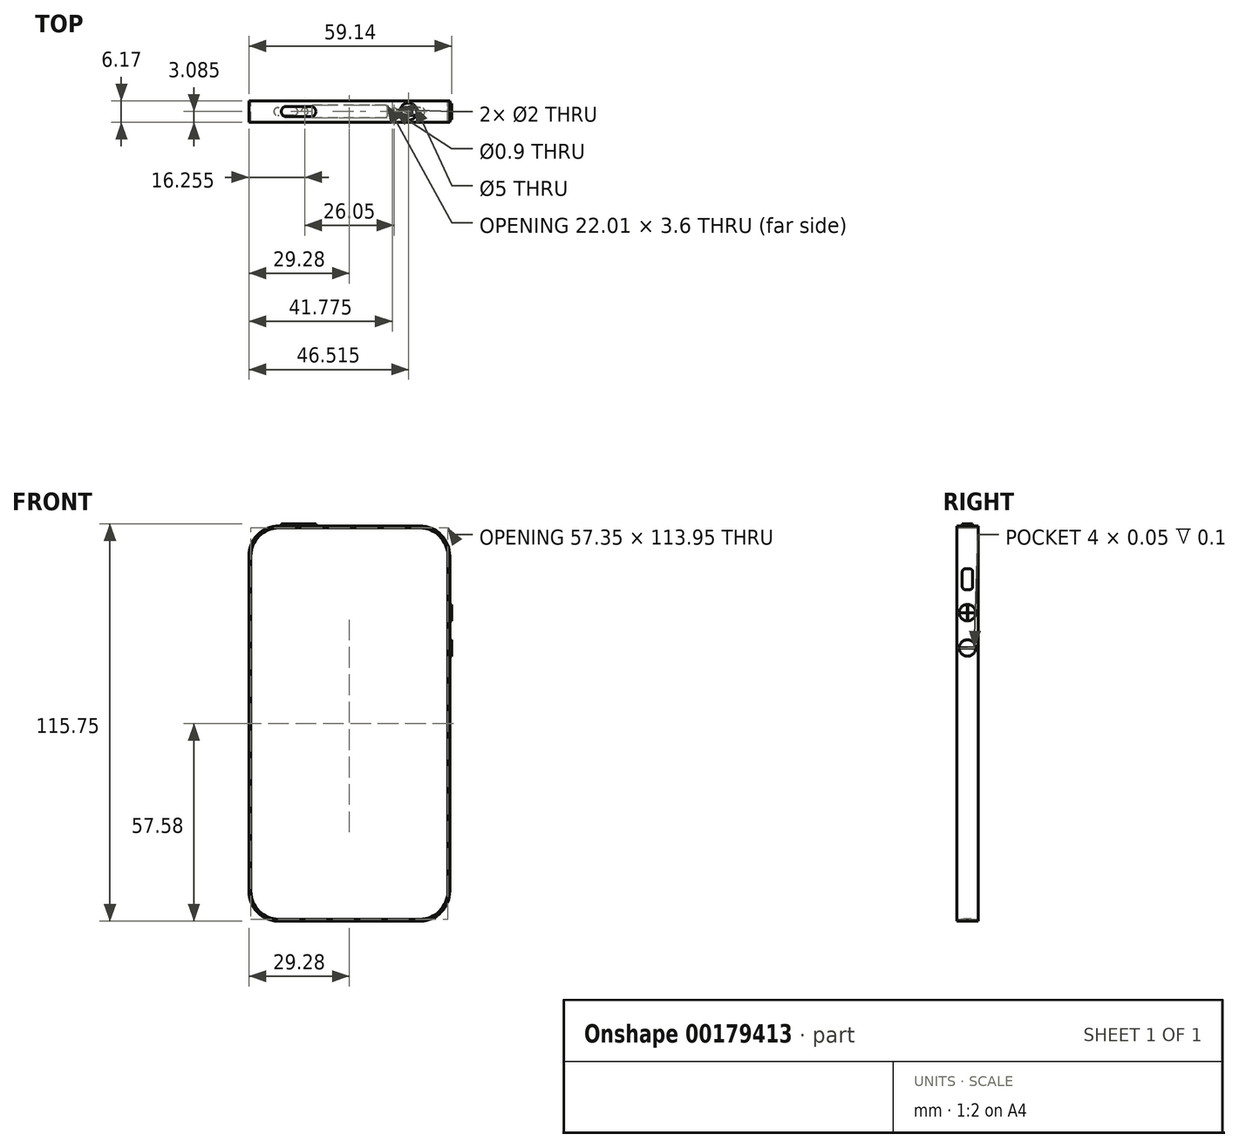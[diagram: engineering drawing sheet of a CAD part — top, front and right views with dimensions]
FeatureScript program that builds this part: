
annotation { "Feature Type Name" : "Feature", "Feature Type Description" : "" }
export const myFeature = defineFeature(function(context is Context, id is Id, definition is map)
    precondition{}
    {
        {
            var Q0;
            Q0=qCreatedBy(makeId("Front.planeOp"),FACE);
            var sketch = newSketch(context, id + "F0", { "sketchPlane" : qUnion([Q0])});
            skLineSegment(sketch, "E0.bottom", {"start": v(20.5, -57.58) * mm, "end": v(-20.5, -57.58) * mm});
            skLineSegment(sketch, "E0.top", {"start": v(20.5, 57.57) * mm, "end": v(-20.5, 57.57) * mm});
            skLineSegment(sketch, "E0.left", {"start": v(29.28, -48.8) * mm, "end": v(29.28, 48.8) * mm});
            skLineSegment(sketch, "E0.right", {"start": v(-29.28, -48.8) * mm, "end": v(-29.28, 48.8) * mm});
            skPoint(sketch, "E0.middle", {"position": v(0, 0) * mm});
            skLineSegment(sketch, "E1.bottom", {"start": v(20.5, -56.98) * mm, "end": v(-20.5, -56.97) * mm});
            skLineSegment(sketch, "E1.top", {"start": v(20.5, 56.98) * mm, "end": v(-20.5, 56.98) * mm});
            skLineSegment(sketch, "E1.left", {"start": v(28.67, -48.8) * mm, "end": v(28.68, 48.8) * mm});
            skLineSegment(sketch, "E1.right", {"start": v(-28.68, -48.8) * mm, "end": v(-28.68, 48.8) * mm});
            skPoint(sketch, "E2.visualSharp", {"position": v(-28.67, 56.97) * mm});
            skArc(sketch, "E2.filletArc", {"start": v(-20.5, 56.97) * mm, "mid": v(-26.28, 54.58) * mm, "end": v(-28.67, 48.8) * mm});
            skPoint(sketch, "E3.visualSharp", {"position": v(-29.28, 57.57) * mm});
            skArc(sketch, "E3.filletArc", {"start": v(-20.5, 57.57) * mm, "mid": v(-26.7, 55) * mm, "end": v(-29.27, 48.8) * mm});
            skPoint(sketch, "E4.visualSharp", {"position": v(28.68, 56.98) * mm});
            skArc(sketch, "E4.filletArc", {"start": v(28.68, 48.8) * mm, "mid": v(26.28, 54.58) * mm, "end": v(20.5, 56.97) * mm});
            skPoint(sketch, "E5.visualSharp", {"position": v(29.28, 57.57) * mm});
            skArc(sketch, "E5.filletArc", {"start": v(29.28, 48.8) * mm, "mid": v(26.7, 55) * mm, "end": v(20.5, 57.57) * mm});
            skPoint(sketch, "E6.visualSharp", {"position": v(-29.28, -57.58) * mm});
            skArc(sketch, "E6.filletArc", {"start": v(-29.28, -48.8) * mm, "mid": v(-26.7, -55) * mm, "end": v(-20.5, -57.57) * mm});
            skPoint(sketch, "E7.visualSharp", {"position": v(-28.68, -56.97) * mm});
            skArc(sketch, "E7.filletArc", {"start": v(-28.68, -48.8) * mm, "mid": v(-26.28, -54.58) * mm, "end": v(-20.5, -56.97) * mm});
            skPoint(sketch, "E8.visualSharp", {"position": v(29.28, -57.58) * mm});
            skArc(sketch, "E8.filletArc", {"start": v(20.5, -57.58) * mm, "mid": v(26.7, -55) * mm, "end": v(29.27, -48.8) * mm});
            skPoint(sketch, "E9.visualSharp", {"position": v(28.67, -56.98) * mm});
            skArc(sketch, "E9.filletArc", {"start": v(20.5, -56.98) * mm, "mid": v(26.28, -54.58) * mm, "end": v(28.67, -48.8) * mm});
            skSolve(sketch);
        }
        {
            var Q0;
            Q0=makeQuery(id+"F0.imprint","IMPRINT",FACE,{"disambiguationData":[TD([[makeQuery(id+"F0.imprint","IMPRINT",EDGE,{"derivedFrom":sQuery(id+"F0.wireOp",EDGE,"E0.bottom")}),-1.0]])]});
            extrude(context, id + "F1", {"entities" : qUnion([Q0]), "depth" : 6.17 * mm});
        }
        {
            var Q0;
            Q0=makeQuery(id+"F1.opExtrude","SWEPT_FACE",FACE,{"disambiguationData":[OSD([sQuery(id+"F0.wireOp",EDGE,"E0.left")])]});
            var sketch = newSketch(context, id + "F2", { "sketchPlane" : qUnion([Q0])});
            skLineSegment(sketch, "E10", {"start": v(-3.08, 48.8) * mm, "end": v(-3.08, -48.8) * mm, "construction": true});
            skCircle(sketch, "E11", {"center": v(-3.08, 32.3) * mm, "radius": 2.4 * mm});
            skCircle(sketch, "E12", {"center": v(-3.08, 22.01) * mm, "radius": 2.4 * mm});
            skLineSegment(sketch, "E13.bottom", {"start": v(-3.83, 45.04) * mm, "end": v(-2.33, 45.04) * mm});
            skLineSegment(sketch, "E13.top", {"start": v(-3.83, 39.04) * mm, "end": v(-2.33, 39.04) * mm});
            skLineSegment(sketch, "E13.left", {"start": v(-4.58, 44.3) * mm, "end": v(-4.58, 39.8) * mm});
            skLineSegment(sketch, "E13.right", {"start": v(-1.58, 44.3) * mm, "end": v(-1.58, 39.8) * mm});
            skPoint(sketch, "E14.visualSharp", {"position": v(-4.58, 45.04) * mm});
            skArc(sketch, "E14.filletArc", {"start": v(-3.83, 45.04) * mm, "mid": v(-4.37, 44.83) * mm, "end": v(-4.59, 44.3) * mm});
            skPoint(sketch, "E15.visualSharp", {"position": v(-1.58, 45.04) * mm});
            skArc(sketch, "E15.filletArc", {"start": v(-1.58, 44.3) * mm, "mid": v(-1.8, 44.83) * mm, "end": v(-2.33, 45.04) * mm});
            skPoint(sketch, "E16.visualSharp", {"position": v(-1.58, 39.04) * mm});
            skArc(sketch, "E16.filletArc", {"start": v(-2.33, 39.04) * mm, "mid": v(-1.8, 39.26) * mm, "end": v(-1.59, 39.8) * mm});
            skPoint(sketch, "E17.visualSharp", {"position": v(-4.58, 39.04) * mm});
            skArc(sketch, "E17.filletArc", {"start": v(-4.58, 39.8) * mm, "mid": v(-4.37, 39.26) * mm, "end": v(-3.83, 39.04) * mm});
            skSolve(sketch);
        }
        {
            var Q0;
            Q0=makeQuery(id+"F2.imprint","IMPRINT",FACE,{"disambiguationData":[TD([[makeQuery(id+"F2.imprint","IMPRINT",EDGE,{"derivedFrom":sQuery(id+"F2.wireOp",EDGE,"E13.bottom")}),-1.0]])]});
            extrude(context, id + "F3", {"entities" : qUnion([Q0]), "operationType" : NewBodyOperationType.REMOVE, "oppositeDirection" : true, "depth" : 0.55 * mm});
        }
        {
            var Q0;
            Q0=makeQuery(id+"F2.imprint","IMPRINT",FACE,{"disambiguationData":[TD([[makeQuery(id+"F2.imprint","IMPRINT",EDGE,{"derivedFrom":sQuery(id+"F2.wireOp",EDGE,"E11")}),1.0]])]});
            var Q1;
            Q1=makeQuery(id+"F2.imprint","IMPRINT",FACE,{"disambiguationData":[TD([[makeQuery(id+"F2.imprint","IMPRINT",EDGE,{"derivedFrom":sQuery(id+"F2.wireOp",EDGE,"E12")}),1.0]])]});
            extrude(context, id + "F4", {"entities" : qUnion([Q0, Q1]), "operationType" : NewBodyOperationType.ADD, "depth" : 0.58 * mm});
        }
        {
            var Q0;
            Q0=makeQuery(id+"F4.opExtrude","CAP_FACE",FACE,{"disambiguationData":[OSD([sQuery(id+"F2.wireOp",EDGE,"E11")])],"isStart":false});
            var sketch = newSketch(context, id + "F5", { "sketchPlane" : qUnion([Q0])});
            skLineSegment(sketch, "E18.bottom", {"start": v(-3.11, 30.3) * mm, "end": v(-3.06, 30.3) * mm});
            skLineSegment(sketch, "E18.top", {"start": v(-3.11, 34.3) * mm, "end": v(-3.06, 34.3) * mm});
            skLineSegment(sketch, "E18.left", {"start": v(-3.11, 30.3) * mm, "end": v(-3.11, 32.27) * mm});
            skLineSegment(sketch, "E18.right", {"start": v(-3.06, 30.3) * mm, "end": v(-3.06, 32.27) * mm});
            skPoint(sketch, "E18.middle", {"position": v(-3.08, 32.3) * mm});
            skLineSegment(sketch, "E19.bottom", {"start": v(-1.08, 32.27) * mm, "end": v(-3.06, 32.27) * mm});
            skLineSegment(sketch, "E19.top", {"start": v(-1.08, 32.32) * mm, "end": v(-3.06, 32.32) * mm});
            skLineSegment(sketch, "E19.left", {"start": v(-1.08, 32.27) * mm, "end": v(-1.08, 32.32) * mm});
            skLineSegment(sketch, "E19.right", {"start": v(-5.08, 32.27) * mm, "end": v(-5.08, 32.32) * mm});
            skLineSegment(sketch, "E20.trimOffspring", {"start": v(-3.11, 32.32) * mm, "end": v(-5.08, 32.32) * mm});
            skLineSegment(sketch, "E21.trimOffspring", {"start": v(-3.11, 32.32) * mm, "end": v(-3.11, 34.3) * mm});
            skLineSegment(sketch, "E22.trimOffspring", {"start": v(-3.06, 32.32) * mm, "end": v(-3.06, 34.3) * mm});
            skLineSegment(sketch, "E23.trimOffspring", {"start": v(-3.11, 32.27) * mm, "end": v(-5.08, 32.27) * mm});
            skSolve(sketch);
        }
        {
            var Q0;
            Q0=makeQuery(id+"F4.opExtrude","CAP_FACE",FACE,{"disambiguationData":[OSD([sQuery(id+"F2.wireOp",EDGE,"E12")])],"isStart":false});
            var sketch = newSketch(context, id + "F6", { "sketchPlane" : qUnion([Q0])});
            skLineSegment(sketch, "E24.bottom", {"start": v(-1.08, 21.99) * mm, "end": v(-5.08, 21.99) * mm});
            skLineSegment(sketch, "E24.top", {"start": v(-1.08, 22.04) * mm, "end": v(-5.08, 22.04) * mm});
            skLineSegment(sketch, "E24.left", {"start": v(-1.08, 21.99) * mm, "end": v(-1.08, 22.04) * mm});
            skLineSegment(sketch, "E24.right", {"start": v(-5.08, 21.99) * mm, "end": v(-5.08, 22.04) * mm});
            skPoint(sketch, "E24.middle", {"position": v(-3.08, 22.01) * mm});
            skSolve(sketch);
        }
        {
            var Q0;
            Q0=makeQuery(id+"F5.imprint","IMPRINT",FACE,{"disambiguationData":[TD([[makeQuery(id+"F5.imprint","IMPRINT",EDGE,{"derivedFrom":sQuery(id+"F5.wireOp",EDGE,"E18.bottom")}),1.0]])]});
            var Q1;
            Q1=makeQuery(id+"F6.imprint","IMPRINT",FACE,{"disambiguationData":[TD([[makeQuery(id+"F6.imprint","IMPRINT",EDGE,{"derivedFrom":sQuery(id+"F6.wireOp",EDGE,"E24.bottom")}),-1.0]])]});
            extrude(context, id + "F7", {"entities" : qUnion([Q0, Q1]), "operationType" : NewBodyOperationType.REMOVE, "oppositeDirection" : true, "depth" : 0.1 * mm});
        }
        {
            var Q0;
            Q0=makeQuery(id+"F1.opExtrude","SWEPT_FACE",FACE,{"disambiguationData":[OSD([sQuery(id+"F0.wireOp",EDGE,"E0.top")])]});
            var sketch = newSketch(context, id + "F8", { "sketchPlane" : qUnion([Q0])});
            skLineSegment(sketch, "E25", {"start": v(20.5, -3.08) * mm, "end": v(-20.5, -3.08) * mm, "construction": true});
            skCircle(sketch, "E26", {"center": v(17.24, -3.08) * mm, "radius": 2.5 * mm});
            skLineSegment(sketch, "E27.bottom", {"start": v(-18.33, -4.59) * mm, "end": v(-11.23, -4.59) * mm});
            skLineSegment(sketch, "E27.top", {"start": v(-18.33, -1.59) * mm, "end": v(-11.23, -1.59) * mm});
            skLineSegment(sketch, "E27.left", {"start": v(-19.83, -3.09) * mm, "end": v(-19.83, -3.09) * mm});
            skLineSegment(sketch, "E27.right", {"start": v(-9.73, -3.09) * mm, "end": v(-9.73, -3.09) * mm});
            skPoint(sketch, "E27.middle", {"position": v(-14.78, -3.09) * mm});
            skCircle(sketch, "E28", {"center": v(12.5, -3.09) * mm, "radius": 0.45 * mm});
            skPoint(sketch, "E29.visualSharp", {"position": v(-9.73, -4.59) * mm});
            skArc(sketch, "E29.filletArc", {"start": v(-11.23, -4.59) * mm, "mid": v(-10.17, -4.15) * mm, "end": v(-9.73, -3.09) * mm});
            skPoint(sketch, "E30.visualSharp", {"position": v(-9.73, -1.59) * mm});
            skArc(sketch, "E30.filletArc", {"start": v(-9.73, -3.09) * mm, "mid": v(-10.17, -2.02) * mm, "end": v(-11.23, -1.59) * mm});
            skPoint(sketch, "E31.visualSharp", {"position": v(-19.83, -4.59) * mm});
            skArc(sketch, "E31.filletArc", {"start": v(-19.83, -3.09) * mm, "mid": v(-19.4, -4.15) * mm, "end": v(-18.33, -4.59) * mm});
            skPoint(sketch, "E32.visualSharp", {"position": v(-19.83, -1.59) * mm});
            skArc(sketch, "E32.filletArc", {"start": v(-18.33, -1.59) * mm, "mid": v(-19.4, -2.02) * mm, "end": v(-19.83, -3.09) * mm});
            skSolve(sketch);
        }
        {
            var Q0;
            Q0=makeQuery(id+"F8.imprint","IMPRINT",FACE,{"disambiguationData":[TD([[makeQuery(id+"F8.imprint","IMPRINT",EDGE,{"derivedFrom":sQuery(id+"F8.wireOp",EDGE,"E26")}),1.0]])]});
            var Q1;
            Q1=makeQuery(id+"F8.imprint","IMPRINT",FACE,{"disambiguationData":[TD([[makeQuery(id+"F8.imprint","IMPRINT",EDGE,{"derivedFrom":sQuery(id+"F8.wireOp",EDGE,"E28")}),1.0]])]});
            var Q2;
            Q2=sQuery(id+"F8.wireOp",EDGE,"E26");
            var Q3;
            Q3=sQuery(id+"F8.wireOp",EDGE,"E28");
            extrude(context, id + "F9", {"entities" : qUnion([Q0, Q1]), "operationType" : NewBodyOperationType.REMOVE, "surfaceEntities" : qUnion([Q2, Q3]), "oppositeDirection" : true, "depth" : 0.6 * mm});
        }
        {
            var Q0;
            Q0=makeQuery(id+"F8.imprint","IMPRINT",FACE,{"disambiguationData":[TD([[makeQuery(id+"F8.imprint","IMPRINT",EDGE,{"derivedFrom":sQuery(id+"F8.wireOp",EDGE,"E27.bottom")}),1.0]])]});
            extrude(context, id + "F10", {"entities" : qUnion([Q0]), "operationType" : NewBodyOperationType.ADD, "depth" : 0.6 * mm});
        }
        {
            var Q0;
            Q0=makeQuery(id+"F1.opExtrude","SWEPT_FACE",FACE,{"disambiguationData":[OSD([sQuery(id+"F0.wireOp",EDGE,"E0.bottom")])]});
            var sketch = newSketch(context, id + "F11", { "sketchPlane" : qUnion([Q0])});
            skLineSegment(sketch, "E33", {"start": v(20.5, 3.08) * mm, "end": v(-20.5, 3.08) * mm, "construction": true});
            skLineSegment(sketch, "E34", {"start": v(0, 6.17) * mm, "end": v(0, 0) * mm, "construction": true});
            skLineSegment(sketch, "E35.bottom", {"start": v(10.5, 1.29) * mm, "end": v(-10.5, 1.28) * mm});
            skLineSegment(sketch, "E35.top", {"start": v(10.5, 4.89) * mm, "end": v(-10.5, 4.88) * mm});
            skLineSegment(sketch, "E35.left", {"start": v(11, 1.78) * mm, "end": v(11, 4.38) * mm});
            skLineSegment(sketch, "E35.right", {"start": v(-11, 1.78) * mm, "end": v(-11, 4.38) * mm});
            skPoint(sketch, "E35.middle", {"position": v(0, 3.08) * mm});
            skCircle(sketch, "E36", {"center": v(-13.03, 3.08) * mm, "radius": 1 * mm});
            skCircle(sketch, "E37", {"center": v(13.02, 3.08) * mm, "radius": 1 * mm});
            skLineSegment(sketch, "E38.bottom", {"start": v(-16.17, 1.94) * mm, "end": v(-20.84, 1.94) * mm});
            skLineSegment(sketch, "E38.top", {"start": v(-16.17, 4.24) * mm, "end": v(-20.84, 4.24) * mm});
            skLineSegment(sketch, "E38.left", {"start": v(-15.02, 3.09) * mm, "end": v(-15.02, 3.08) * mm});
            skLineSegment(sketch, "E38.right", {"start": v(-21.99, 3.09) * mm, "end": v(-21.99, 3.08) * mm});
            skPoint(sketch, "E38.middle", {"position": v(-18.5, 3.08) * mm});
            skLineSegment(sketch, "E39.bottom", {"start": v(20.83, 1.94) * mm, "end": v(16.16, 1.94) * mm});
            skLineSegment(sketch, "E39.top", {"start": v(20.83, 4.24) * mm, "end": v(16.16, 4.24) * mm});
            skLineSegment(sketch, "E39.left", {"start": v(21.98, 3.09) * mm, "end": v(21.98, 3.09) * mm});
            skLineSegment(sketch, "E39.right", {"start": v(15.01, 3.09) * mm, "end": v(15.01, 3.09) * mm});
            skPoint(sketch, "E39.middle", {"position": v(18.5, 3.08) * mm});
            skPoint(sketch, "E40.visualSharp", {"position": v(-15.02, 4.24) * mm});
            skArc(sketch, "E40.filletArc", {"start": v(-15.02, 3.08) * mm, "mid": v(-15.35, 3.9) * mm, "end": v(-16.17, 4.24) * mm});
            skPoint(sketch, "E41.visualSharp", {"position": v(-15.02, 1.94) * mm});
            skArc(sketch, "E41.filletArc", {"start": v(-16.17, 1.94) * mm, "mid": v(-15.35, 2.27) * mm, "end": v(-15.02, 3.09) * mm});
            skPoint(sketch, "E42.visualSharp", {"position": v(-21.99, 1.94) * mm});
            skArc(sketch, "E42.filletArc", {"start": v(-21.99, 3.09) * mm, "mid": v(-21.65, 2.27) * mm, "end": v(-20.84, 1.94) * mm});
            skPoint(sketch, "E43.visualSharp", {"position": v(-21.99, 4.24) * mm});
            skArc(sketch, "E43.filletArc", {"start": v(-20.84, 4.24) * mm, "mid": v(-21.65, 3.9) * mm, "end": v(-21.99, 3.08) * mm});
            skPoint(sketch, "E44.visualSharp", {"position": v(21.98, 4.24) * mm});
            skArc(sketch, "E44.filletArc", {"start": v(21.98, 3.09) * mm, "mid": v(21.65, 3.9) * mm, "end": v(20.83, 4.24) * mm});
            skPoint(sketch, "E45.visualSharp", {"position": v(21.98, 1.94) * mm});
            skArc(sketch, "E45.filletArc", {"start": v(20.83, 1.94) * mm, "mid": v(21.65, 2.27) * mm, "end": v(21.98, 3.09) * mm});
            skPoint(sketch, "E46.visualSharp", {"position": v(15.01, 1.94) * mm});
            skArc(sketch, "E46.filletArc", {"start": v(15.01, 3.09) * mm, "mid": v(15.35, 2.27) * mm, "end": v(16.16, 1.94) * mm});
            skPoint(sketch, "E47.visualSharp", {"position": v(15.01, 4.23) * mm});
            skArc(sketch, "E47.filletArc", {"start": v(16.16, 4.24) * mm, "mid": v(15.35, 3.9) * mm, "end": v(15.01, 3.09) * mm});
            skPoint(sketch, "E48.visualSharp", {"position": v(-11, 4.89) * mm});
            skArc(sketch, "E48.filletArc", {"start": v(-10.5, 4.89) * mm, "mid": v(-10.86, 4.74) * mm, "end": v(-11, 4.38) * mm});
            skPoint(sketch, "E49.visualSharp", {"position": v(-11, 1.29) * mm});
            skArc(sketch, "E49.filletArc", {"start": v(-11, 1.78) * mm, "mid": v(-10.86, 1.43) * mm, "end": v(-10.5, 1.28) * mm});
            skPoint(sketch, "E50.visualSharp", {"position": v(11, 4.89) * mm});
            skArc(sketch, "E50.filletArc", {"start": v(11, 4.38) * mm, "mid": v(10.86, 4.74) * mm, "end": v(10.5, 4.89) * mm});
            skPoint(sketch, "E51.visualSharp", {"position": v(11, 1.29) * mm});
            skArc(sketch, "E51.filletArc", {"start": v(10.5, 1.28) * mm, "mid": v(10.86, 1.43) * mm, "end": v(11, 1.78) * mm});
            skSolve(sketch);
        }
        {
            var Q0;
            Q0 = qSketchRegion(id + "F11", true);
            extrude(context, id + "F12", {"entities" : qUnion([Q0]), "operationType" : NewBodyOperationType.REMOVE, "endBound" : BoundingType.UP_TO_NEXT, "oppositeDirection" : true, "depth" : 0.6 * mm});
        }
    });
